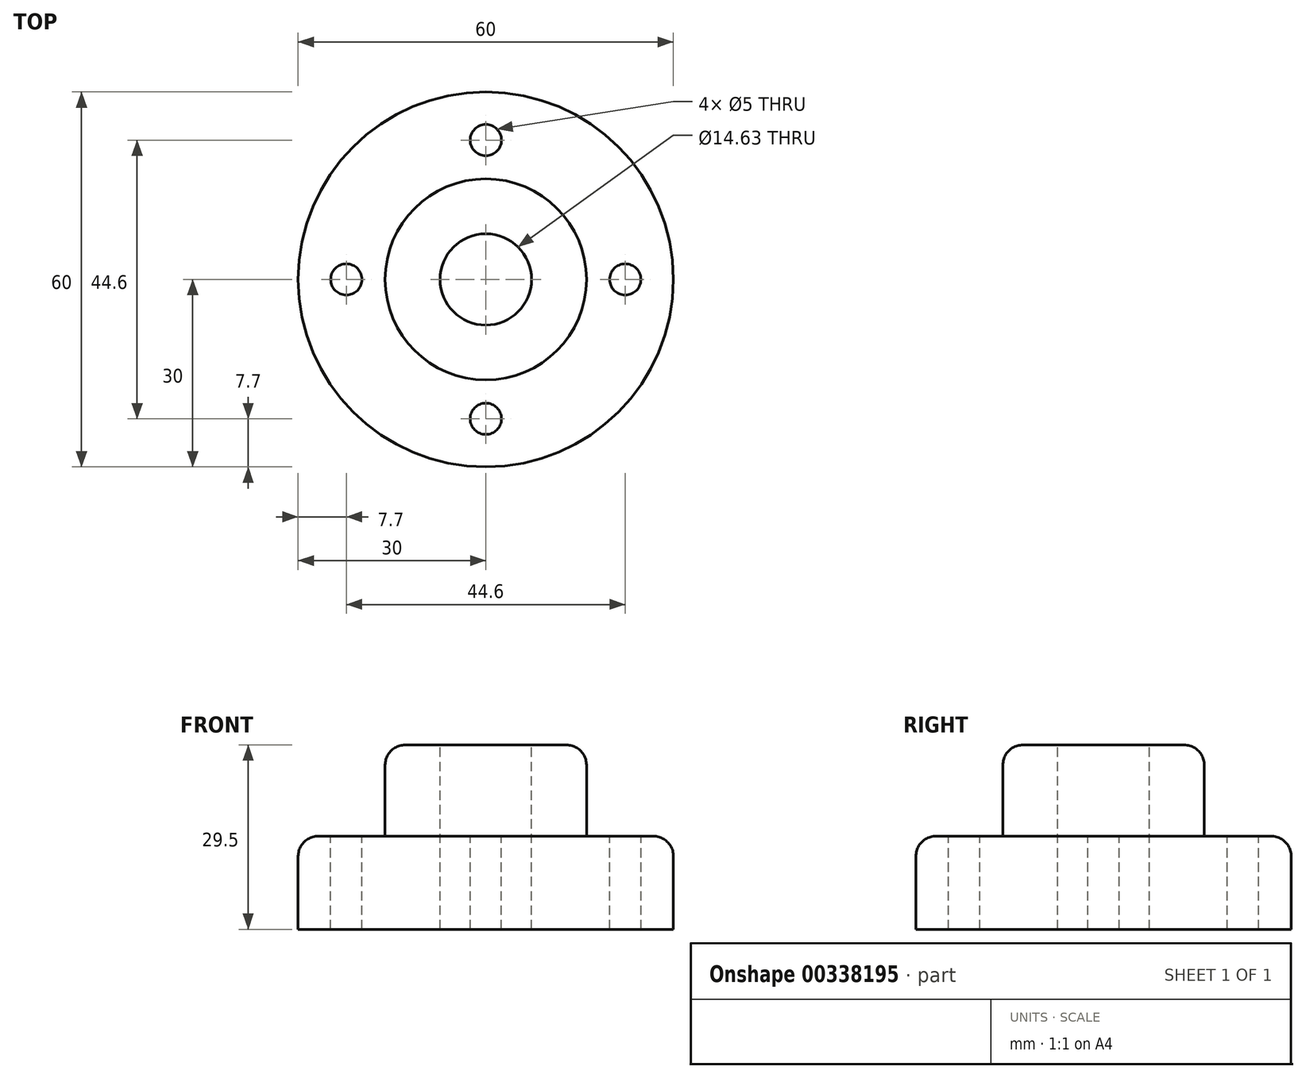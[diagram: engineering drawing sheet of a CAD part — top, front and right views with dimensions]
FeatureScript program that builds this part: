
annotation { "Feature Type Name" : "Feature", "Feature Type Description" : "" }
export const myFeature = defineFeature(function(context is Context, id is Id, definition is map)
    precondition{}
    {
        {
            var Q0;
            Q0=qCreatedBy(makeId("Top.planeOp"),FACE);
            var sketch = newSketch(context, id + "F0", { "sketchPlane" : qUnion([Q0])});
            skCircle(sketch, "E0", {"center": v(0, 0) * mm, "radius": 30 * mm});
            skSolve(sketch);
        }
        {
            var Q0;
            Q0 = qSketchRegion(id + "F0", true);
            extrude(context, id + "F1", {"entities" : qUnion([Q0]), "depth" : 14.9 * mm});
        }
        {
            var Q0;
            Q0=makeQuery(id+"F1.opExtrude","CAP_FACE",FACE,{"disambiguationData":[OSD([sQuery(id+"F0.wireOp",EDGE,"E0")])],"isStart":false});
            cPlane(context, id + "F2", {"entities" : qUnion([Q0]), "cplaneType" : CPlaneType.OFFSET, "offset" : 0 * mm, "width" : 150 * mm, "height" : 150 * mm});
        }
        {
            var Q0;
            Q0=qCreatedBy(id+"F2.planeOp",FACE);
            var sketch = newSketch(context, id + "F3", { "sketchPlane" : qUnion([Q0])});
            skCircle(sketch, "E1", {"center": v(0, 0) * mm, "radius": 16.1 * mm});
            skSolve(sketch);
        }
        {
            var Q0;
            Q0 = qSketchRegion(id + "F3", true);
            extrude(context, id + "F4", {"entities" : qUnion([Q0]), "operationType" : NewBodyOperationType.ADD, "depth" : 14.6 * mm});
        }
        {
            var Q0;
            Q0=qCreatedBy(id+"F2.planeOp",FACE);
            var sketch = newSketch(context, id + "F5", { "sketchPlane" : qUnion([Q0])});
            skCircle(sketch, "E2", {"center": v(-22.3, 0) * mm, "radius": 2.5 * mm});
            skCircle(sketch, "E3", {"center": v(0, 22.3) * mm, "radius": 2.5 * mm});
            skCircle(sketch, "E4", {"center": v(22.3, 0) * mm, "radius": 2.5 * mm});
            skCircle(sketch, "E5", {"center": v(0, -22.3) * mm, "radius": 2.5 * mm});
            skSolve(sketch);
        }
        {
            var Q0;
            Q0 = qSketchRegion(id + "F5", true);
            extrude(context, id + "F6", {"entities" : qUnion([Q0]), "operationType" : NewBodyOperationType.REMOVE, "oppositeDirection" : true, "depth" : 25 * mm});
        }
        {
            var Q0;
            Q0=makeQuery(id+"F1.opExtrude","CAP_EDGE",EDGE,{"disambiguationData":[OSD([sQuery(id+"F0.wireOp",EDGE,"E0")])],"isStart":false});
            var Q1;
            Q1=makeQuery(id+"F4.opExtrude","CAP_EDGE",EDGE,{"disambiguationData":[OSD([sQuery(id+"F3.wireOp",EDGE,"E1")])],"isStart":false});
            fillet(context, id + "F7", {"entities" : qUnion([Q0, Q1]), "radius" : 3.2 * mm, "tangentPropagation" : true, "allowEdgeOverflow" : false});
        }
        {
            var Q0;
            Q0=makeQuery(id+"F4.opExtrude","CAP_FACE",FACE,{"disambiguationData":[OSD([sQuery(id+"F3.wireOp",EDGE,"E1")])],"isStart":false});
            cPlane(context, id + "F8", {"entities" : qUnion([Q0]), "cplaneType" : CPlaneType.OFFSET, "offset" : 0 * mm, "width" : 150 * mm, "height" : 150 * mm});
        }
        {
            var Q0;
            Q0=qCreatedBy(id+"F8.planeOp",FACE);
            var sketch = newSketch(context, id + "F9", { "sketchPlane" : qUnion([Q0])});
            skCircle(sketch, "E6", {"center": v(0, 0) * mm, "radius": 7.32 * mm});
            skSolve(sketch);
        }
        {
            var Q0;
            Q0 = qSketchRegion(id + "F9", true);
            extrude(context, id + "F10", {"entities" : qUnion([Q0]), "operationType" : NewBodyOperationType.REMOVE, "oppositeDirection" : true, "depth" : 50 * mm});
        }
    });
